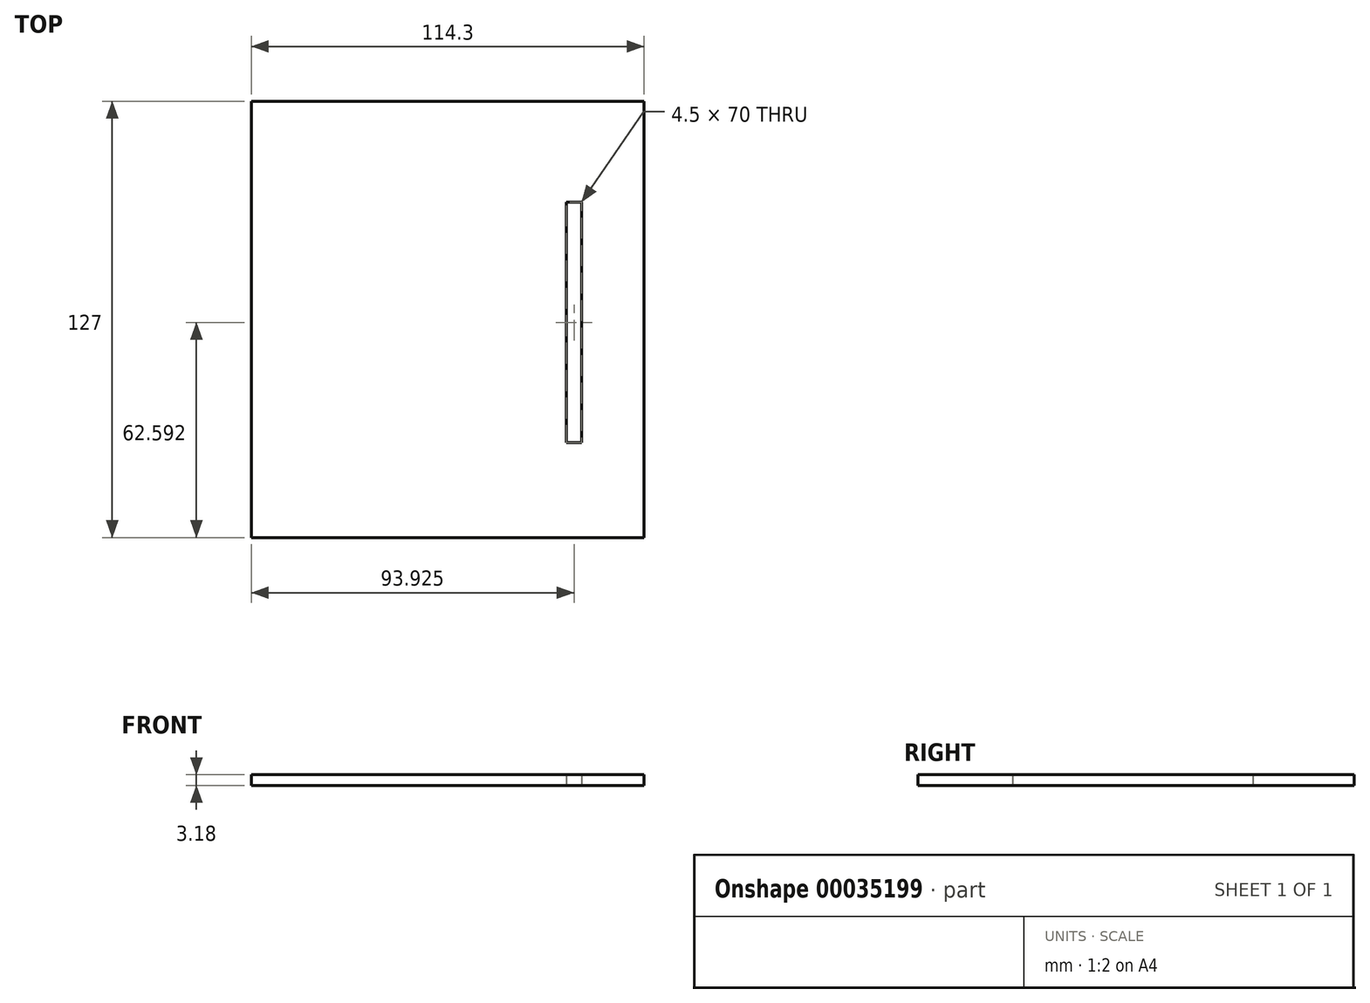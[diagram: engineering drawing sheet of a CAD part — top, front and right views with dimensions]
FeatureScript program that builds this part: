
annotation { "Feature Type Name" : "Feature", "Feature Type Description" : "" }
export const myFeature = defineFeature(function(context is Context, id is Id, definition is map)
    precondition{}
    {
        {
            var Q0;
            Q0=qCreatedBy(makeId("Top.planeOp"),FACE);
            var sketch = newSketch(context, id + "F0", { "sketchPlane" : qUnion([Q0])});
            skLineSegment(sketch, "E0.bottom", {"start": v(-55, 71.24) * mm, "end": v(59.3, 71.24) * mm});
            skLineSegment(sketch, "E0.top", {"start": v(-55, -55.76) * mm, "end": v(59.3, -55.76) * mm});
            skLineSegment(sketch, "E0.left", {"start": v(-55, 71.24) * mm, "end": v(-55, -55.76) * mm});
            skLineSegment(sketch, "E0.right", {"start": v(59.3, 71.24) * mm, "end": v(59.3, -55.76) * mm});
            skLineSegment(sketch, "E1.rect.bottom", {"start": v(36.67, 41.83) * mm, "end": v(41.17, 41.83) * mm});
            skLineSegment(sketch, "E1.rect.top", {"start": v(36.67, -28.17) * mm, "end": v(41.17, -28.17) * mm});
            skLineSegment(sketch, "E1.rect.left", {"start": v(36.67, 41.83) * mm, "end": v(36.67, -28.17) * mm});
            skLineSegment(sketch, "E1.rect.right", {"start": v(41.17, 41.83) * mm, "end": v(41.17, -28.17) * mm});
            skPoint(sketch, "E1.rect.middle", {"position": v(38.92, 6.83) * mm});
            skSolve(sketch);
        }
        {
            var Q0;
            Q0=makeQuery(id+"F0.imprint","IMPRINT",FACE,{"disambiguationData":[TD([[makeQuery(id+"F0.imprint","IMPRINT",EDGE,{"derivedFrom":sQuery(id+"F0.wireOp",EDGE,"E0.bottom")}),-1.0]])]});
            extrude(context, id + "F1", {"entities" : qUnion([Q0]), "depth" : 3.18 * mm});
        }
    });
